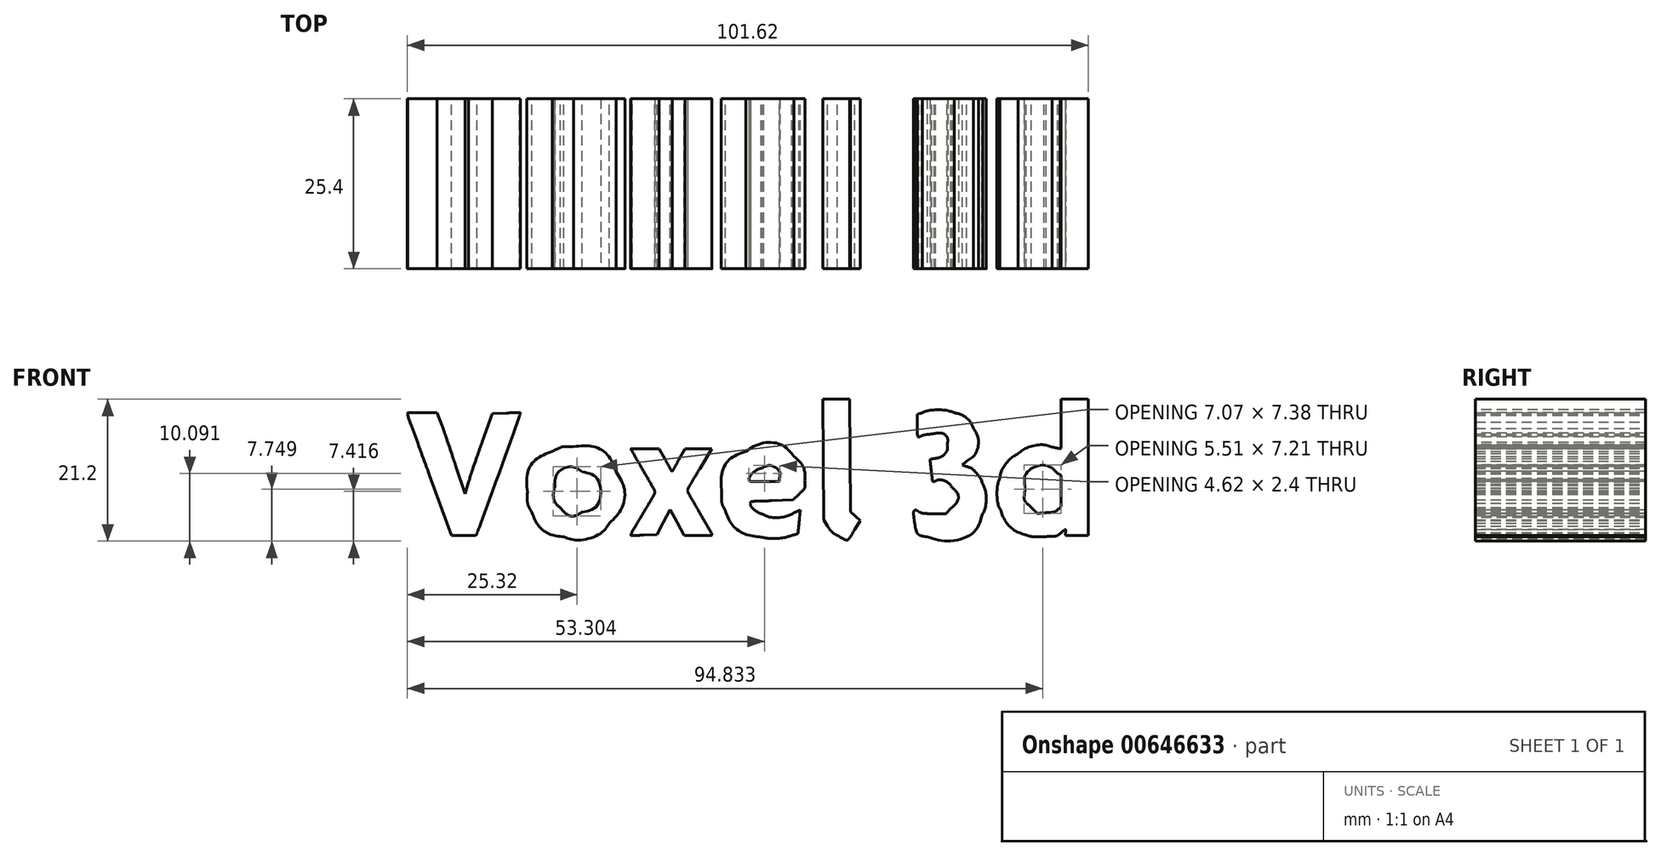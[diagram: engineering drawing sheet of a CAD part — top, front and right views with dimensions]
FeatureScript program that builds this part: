
annotation { "Feature Type Name" : "Feature", "Feature Type Description" : "" }
export const myFeature = defineFeature(function(context is Context, id is Id, definition is map)
    precondition{}
    {
        {
            var Q0;
            Q0=qCreatedBy(makeId("Front.planeOp"),FACE);
            var sketch = newSketch(context, id + "F0", { "sketchPlane" : qUnion([Q0])});
            skFitSpline(sketch, "E0", {"points": [v(-27.45, -20.66) * mm, v(-29.62, -20.2) * mm, v(-31.25, -18.97) * mm, v(-32.22, -17.03) * mm]});
            skFitSpline(sketch, "E1", {"points": [v(-32.22, -17.03) * mm, v(-32.8, -15.86) * mm, v(-32.9, -15.42) * mm, v(-32.9, -13.96) * mm]});
            skFitSpline(sketch, "E2", {"points": [v(-32.9, -13.96) * mm, v(-32.89, -11.11) * mm, v(-31.65, -9.09) * mm, v(-29.17, -7.87) * mm]});
            skFitSpline(sketch, "E3", {"points": [v(-29.17, -7.87) * mm, v(-27.91, -7.25) * mm, v(-27.48, -7.15) * mm, v(-26, -7.15) * mm]});
            skFitSpline(sketch, "E4", {"points": [v(-26, -7.15) * mm, v(-23.06, -7.15) * mm, v(-20.9, -8.43) * mm, v(-19.68, -10.91) * mm]});
            skFitSpline(sketch, "E5", {"points": [v(-19.68, -10.91) * mm, v(-18.45, -13.43) * mm, v(-18.83, -16.4) * mm, v(-20.68, -18.58) * mm]});
            skFitSpline(sketch, "E6", {"points": [v(-20.68, -18.58) * mm, v(-21.99, -20.12) * mm, v(-25.23, -21.12) * mm, v(-27.45, -20.66) * mm]});
            skFitSpline(sketch, "E7", {"points": [v(-24.71, -16.94) * mm, v(-22.4, -15.85) * mm, v(-22.43, -12.03) * mm, v(-24.75, -10.93) * mm]});
            skFitSpline(sketch, "E8", {"points": [v(-24.75, -10.93) * mm, v(-26.41, -10.14) * mm, v(-28.44, -11.17) * mm, v(-28.78, -12.97) * mm]});
            skFitSpline(sketch, "E9", {"points": [v(-28.78, -12.97) * mm, v(-29.04, -14.33) * mm, v(-28.75, -15.5) * mm, v(-27.96, -16.3) * mm]});
            skFitSpline(sketch, "E10", {"points": [v(-27.96, -16.3) * mm, v(-26.97, -17.33) * mm, v(-25.95, -17.53) * mm, v(-24.71, -16.94) * mm]});
            skFitSpline(sketch, "E11", {"points": [v(1.98, -20.67) * mm, v(-0.45, -20.22) * mm, v(-2.35, -18.82) * mm, v(-3.37, -16.72) * mm]});
            skFitSpline(sketch, "E12", {"points": [v(-3.37, -16.72) * mm, v(-3.8, -15.85) * mm, v(-3.9, -15.28) * mm, v(-3.9, -13.94) * mm]});
            skFitSpline(sketch, "E13", {"points": [v(-3.9, -13.94) * mm, v(-3.87, -11.07) * mm, v(-2.66, -9.03) * mm, v(-0.3, -7.86) * mm]});
            skFitSpline(sketch, "E14", {"points": [v(-0.3, -7.86) * mm, v(2.2, -6.63) * mm, v(5.12, -6.94) * mm, v(6.9, -8.64) * mm]});
            skFitSpline(sketch, "E15", {"points": [v(6.9, -8.64) * mm, v(7.92, -9.6) * mm, v(8.49, -10.9) * mm, v(8.5, -12.27) * mm]});
            skFitSpline(sketch, "E16", {"points": [v(8.5, -12.27) * mm, v(8.5, -13.3) * mm, v(8.42, -13.49) * mm, v(7.62, -14.26) * mm]});
            skFitSpline(sketch, "E17", {"points": [v(3.6, -15.23) * mm, v(1.4, -15.31) * mm, v(0.44, -15.43) * mm, v(0.44, -15.61) * mm]});
            skFitSpline(sketch, "E18", {"points": [v(0.44, -15.61) * mm, v(0.44, -16) * mm, v(1.58, -17.01) * mm, v(2.35, -17.3) * mm]});
            skFitSpline(sketch, "E19", {"points": [v(2.35, -17.3) * mm, v(3.41, -17.7) * mm, v(5.69, -17.6) * mm, v(6.84, -17.09) * mm]});
            skLineSegment(sketch, "E20", {"start": v(7.62, -14.26) * mm, "end": v(6.74, -15.12) * mm});
            skLineSegment(sketch, "E21", {"start": v(6.74, -15.12) * mm, "end": v(3.6, -15.23) * mm});
            skFitSpline(sketch, "E22", {"points": [v(7.72, -17.92) * mm, v(7.48, -20.1) * mm, v(7.45, -20.17) * mm, v(6.54, -20.43) * mm]});
            skFitSpline(sketch, "E23", {"points": [v(6.54, -20.43) * mm, v(5.34, -20.77) * mm, v(3.18, -20.88) * mm, v(1.98, -20.67) * mm]});
            skLineSegment(sketch, "E24", {"start": v(6.84, -17.09) * mm, "end": v(7.86, -16.64) * mm});
            skLineSegment(sketch, "E25", {"start": v(7.86, -16.64) * mm, "end": v(7.72, -17.92) * mm});
            skFitSpline(sketch, "E26", {"points": [v(4.7, -11.98) * mm, v(4.7, -10.83) * mm, v(3.31, -9.97) * mm, v(2.1, -10.37) * mm]});
            skFitSpline(sketch, "E27", {"points": [v(2.1, -10.37) * mm, v(1.4, -10.6) * mm, v(0.22, -11.73) * mm, v(0.22, -12.17) * mm]});
            skFitSpline(sketch, "E28", {"points": [v(0.22, -12.17) * mm, v(0.22, -12.28) * mm, v(1.23, -12.38) * mm, v(2.46, -12.38) * mm]});
            skFitSpline(sketch, "E29", {"points": [v(2.46, -12.38) * mm, v(4.45, -12.38) * mm, v(4.7, -12.33) * mm, v(4.7, -11.98) * mm]});
            skFitSpline(sketch, "E30", {"points": [v(13.37, -20.42) * mm, v(12.9, -20.17) * mm, v(12.25, -19.56) * mm, v(11.91, -19.04) * mm]});
            skFitSpline(sketch, "E31", {"points": [v(15.96, -19.55) * mm, v(15, -21.03) * mm, v(14.7, -21.13) * mm, v(13.37, -20.42) * mm]});
            skLineSegment(sketch, "E32", {"start": v(11.91, -19.04) * mm, "end": v(11.3, -18.12) * mm});
            skLineSegment(sketch, "E33", {"start": v(11.3, -18.12) * mm, "end": v(11.23, -9.1) * mm});
            skLineSegment(sketch, "E34", {"start": v(11.23, -9.1) * mm, "end": v(11.17, -0.07) * mm});
            skLineSegment(sketch, "E35", {"start": v(11.17, -0.07) * mm, "end": v(13.18, -0.07) * mm});
            skLineSegment(sketch, "E36", {"start": v(13.18, -0.07) * mm, "end": v(15.2, -0.07) * mm});
            skLineSegment(sketch, "E37", {"start": v(15.2, -0.07) * mm, "end": v(15.26, -8.48) * mm});
            skLineSegment(sketch, "E38", {"start": v(15.26, -8.48) * mm, "end": v(15.33, -16.89) * mm});
            skLineSegment(sketch, "E39", {"start": v(15.33, -16.89) * mm, "end": v(16.07, -17.55) * mm});
            skLineSegment(sketch, "E40", {"start": v(16.07, -17.55) * mm, "end": v(16.81, -18.22) * mm});
            skLineSegment(sketch, "E41", {"start": v(16.81, -18.22) * mm, "end": v(15.96, -19.55) * mm});
            skFitSpline(sketch, "E42", {"points": [v(26.76, -20.65) * mm, v(26.16, -20.55) * mm, v(25.58, -20.37) * mm, v(25.46, -20.25) * mm]});
            skFitSpline(sketch, "E43", {"points": [v(25.46, -20.25) * mm, v(25.24, -20.03) * mm, v(24.77, -16.84) * mm, v(24.93, -16.68) * mm]});
            skFitSpline(sketch, "E44", {"points": [v(24.93, -16.68) * mm, v(24.98, -16.63) * mm, v(25.26, -16.72) * mm, v(25.54, -16.88) * mm]});
            skFitSpline(sketch, "E45", {"points": [v(25.54, -16.88) * mm, v(25.84, -17.04) * mm, v(26.84, -17.17) * mm, v(27.82, -17.18) * mm]});
            skFitSpline(sketch, "E46", {"points": [v(27.82, -17.18) * mm, v(29.56, -17.19) * mm, v(29.57, -17.18) * mm, v(30.34, -16.35) * mm]});
            skFitSpline(sketch, "E47", {"points": [v(30.34, -16.35) * mm, v(31.3, -15.3) * mm, v(31.37, -14.29) * mm, v(30.53, -13.3) * mm]});
            skFitSpline(sketch, "E48", {"points": [v(30.53, -13.3) * mm, v(29.93, -12.58) * mm, v(28.73, -12.11) * mm, v(28, -12.3) * mm]});
            skFitSpline(sketch, "E49", {"points": [v(28, -12.3) * mm, v(27.65, -12.4) * mm, v(27.57, -12.24) * mm, v(27.45, -11.22) * mm]});
            skFitSpline(sketch, "E50", {"points": [v(27.45, -11.22) * mm, v(27.21, -9.28) * mm, v(27.25, -9.08) * mm, v(27.84, -8.93) * mm]});
            skFitSpline(sketch, "E51", {"points": [v(27.84, -8.93) * mm, v(28.85, -8.68) * mm, v(29.76, -7.7) * mm, v(29.76, -6.89) * mm]});
            skFitSpline(sketch, "E52", {"points": [v(29.76, -6.89) * mm, v(29.76, -5.75) * mm, v(28.87, -5.14) * mm, v(27.41, -5.28) * mm]});
            skFitSpline(sketch, "E53", {"points": [v(27.41, -5.28) * mm, v(26.8, -5.33) * mm, v(26.13, -5.45) * mm, v(25.93, -5.53) * mm]});
            skFitSpline(sketch, "E54", {"points": [v(25.93, -5.53) * mm, v(25.48, -5.72) * mm, v(25.3, -5.12) * mm, v(25.29, -3.5) * mm]});
            skFitSpline(sketch, "E55", {"points": [v(25.29, -3.5) * mm, v(25.28, -2.38) * mm, v(25.3, -2.33) * mm, v(26.05, -2.09) * mm]});
            skFitSpline(sketch, "E56", {"points": [v(26.05, -2.09) * mm, v(27.1, -1.74) * mm, v(29.66, -1.74) * mm, v(30.81, -2.09) * mm]});
            skFitSpline(sketch, "E57", {"points": [v(30.81, -2.09) * mm, v(32, -2.44) * mm, v(33.17, -3.4) * mm, v(33.65, -4.4) * mm]});
            skFitSpline(sketch, "E58", {"points": [v(33.65, -4.4) * mm, v(34.4, -6) * mm, v(33.96, -8.23) * mm, v(32.65, -9.33) * mm]});
            skFitSpline(sketch, "E59", {"points": [v(32.68, -10.14) * mm, v(33.48, -10.47) * mm, v(34.62, -11.73) * mm, v(35.05, -12.74) * mm]});
            skFitSpline(sketch, "E60", {"points": [v(35.05, -12.74) * mm, v(35.5, -13.81) * mm, v(35.43, -16.32) * mm, v(34.93, -17.42) * mm]});
            skFitSpline(sketch, "E61", {"points": [v(34.93, -17.42) * mm, v(33.84, -19.83) * mm, v(30.22, -21.26) * mm, v(26.76, -20.65) * mm]});
            skLineSegment(sketch, "E62", {"start": v(32.65, -9.33) * mm, "end": v(32.02, -9.87) * mm});
            skLineSegment(sketch, "E63", {"start": v(32.02, -9.87) * mm, "end": v(32.68, -10.14) * mm});
            skFitSpline(sketch, "E64", {"points": [v(41.56, -20.35) * mm, v(39.93, -19.74) * mm, v(38.42, -18.26) * mm, v(37.71, -16.57) * mm]});
            skFitSpline(sketch, "E65", {"points": [v(37.71, -16.57) * mm, v(37.32, -15.63) * mm, v(37.26, -13.12) * mm, v(37.6, -11.89) * mm]});
            skFitSpline(sketch, "E66", {"points": [v(37.6, -11.89) * mm, v(37.96, -10.6) * mm, v(39.17, -8.98) * mm, v(40.36, -8.2) * mm]});
            skFitSpline(sketch, "E67", {"points": [v(40.36, -8.2) * mm, v(41.73, -7.3) * mm, v(43.95, -6.87) * mm, v(45.43, -7.21) * mm]});
            skFitSpline(sketch, "E68", {"points": [v(45.43, -7.21) * mm, v(45.98, -7.34) * mm, v(46.5, -7.44) * mm, v(46.6, -7.45) * mm]});
            skFitSpline(sketch, "E69", {"points": [v(46.6, -7.45) * mm, v(46.7, -7.45) * mm, v(46.77, -5.8) * mm, v(46.77, -3.76) * mm]});
            skLineSegment(sketch, "E70", {"start": v(26.76, -20.65) * mm, "end": v(26.76, -20.65) * mm});
            skFitSpline(sketch, "E71", {"points": [v(49.12, -20.43) * mm, v(47.58, -20.43) * mm, v(47.44, -20.4) * mm, v(47.44, -19.98) * mm]});
            skFitSpline(sketch, "E72", {"points": [v(47.44, -19.98) * mm, v(47.44, -19.53) * mm, v(47.42, -19.53) * mm, v(46.75, -20.03) * mm]});
            skFitSpline(sketch, "E73", {"points": [v(46.75, -20.03) * mm, v(46.18, -20.45) * mm, v(45.73, -20.55) * mm, v(44.23, -20.6) * mm]});
            skFitSpline(sketch, "E74", {"points": [v(44.23, -20.6) * mm, v(43.09, -20.64) * mm, v(42.09, -20.54) * mm, v(41.56, -20.35) * mm]});
            skLineSegment(sketch, "E75", {"start": v(46.77, -3.76) * mm, "end": v(46.77, -0.07) * mm});
            skLineSegment(sketch, "E76", {"start": v(46.77, -0.07) * mm, "end": v(48.78, -0.07) * mm});
            skLineSegment(sketch, "E77", {"start": v(48.78, -0.07) * mm, "end": v(50.8, -0.07) * mm});
            skLineSegment(sketch, "E78", {"start": v(50.8, -0.07) * mm, "end": v(50.8, -10.25) * mm});
            skLineSegment(sketch, "E79", {"start": v(50.8, -10.25) * mm, "end": v(50.8, -20.43) * mm});
            skLineSegment(sketch, "E80", {"start": v(50.8, -20.43) * mm, "end": v(49.12, -20.43) * mm});
            skFitSpline(sketch, "E81", {"points": [v(46.31, -16.52) * mm, v(46.71, -16.16) * mm, v(46.77, -15.84) * mm, v(46.77, -13.8) * mm]});
            skFitSpline(sketch, "E82", {"points": [v(46.77, -13.8) * mm, v(46.77, -11.65) * mm, v(46.73, -11.47) * mm, v(46.26, -11.18) * mm]});
            skFitSpline(sketch, "E83", {"points": [v(46.26, -11.18) * mm, v(44.25, -9.92) * mm, v(41.57, -11.13) * mm, v(41.38, -13.39) * mm]});
            skFitSpline(sketch, "E84", {"points": [v(41.38, -13.39) * mm, v(41.26, -14.9) * mm, v(41.4, -15.34) * mm, v(42.3, -16.23) * mm]});
            skFitSpline(sketch, "E85", {"points": [v(42.3, -16.23) * mm, v(43.17, -17.11) * mm, v(43.21, -17.13) * mm, v(44.52, -17.03) * mm]});
            skFitSpline(sketch, "E86", {"points": [v(44.52, -17.03) * mm, v(45.4, -16.97) * mm, v(46.01, -16.8) * mm, v(46.31, -16.52) * mm]});
            skFitSpline(sketch, "E87", {"points": [v(-47.53, -11.42) * mm, v(-49.33, -6.47) * mm, v(-50.8, -2.34) * mm, v(-50.8, -2.25) * mm]});
            skFitSpline(sketch, "E88", {"points": [v(-50.8, -2.25) * mm, v(-50.8, -2.16) * mm, v(-49.8, -2.08) * mm, v(-48.59, -2.08) * mm]});
            skFitSpline(sketch, "E89", {"points": [v(-45.66, -4.04) * mm, v(-45.26, -5.12) * mm, v(-44.33, -7.85) * mm, v(-43.57, -10.1) * mm]});
            skLineSegment(sketch, "E90", {"start": v(-48.59, -2.08) * mm, "end": v(-46.37, -2.08) * mm});
            skLineSegment(sketch, "E91", {"start": v(-46.37, -2.08) * mm, "end": v(-45.66, -4.04) * mm});
            skFitSpline(sketch, "E92", {"points": [v(-41.68, -12.46) * mm, v(-41.39, -11.49) * mm, v(-40.48, -8.78) * mm, v(-39.66, -6.45) * mm]});
            skLineSegment(sketch, "E93", {"start": v(-43.57, -10.1) * mm, "end": v(-42.2, -14.21) * mm});
            skLineSegment(sketch, "E94", {"start": v(-42.2, -14.21) * mm, "end": v(-41.68, -12.46) * mm});
            skFitSpline(sketch, "E95", {"points": [v(-36.06, -2.13) * mm, v(-34.14, -2.07) * mm, v(-33.97, -2.1) * mm, v(-34.07, -2.46) * mm]});
            skFitSpline(sketch, "E96", {"points": [v(-34.07, -2.46) * mm, v(-34.15, -2.77) * mm, v(-39.95, -18.83) * mm, v(-40.45, -20.15) * mm]});
            skFitSpline(sketch, "E97", {"points": [v(-40.45, -20.15) * mm, v(-40.52, -20.35) * mm, v(-41.13, -20.43) * mm, v(-42.4, -20.43) * mm]});
            skLineSegment(sketch, "E98", {"start": v(-39.66, -6.45) * mm, "end": v(-38.16, -2.2) * mm});
            skLineSegment(sketch, "E99", {"start": v(-38.16, -2.2) * mm, "end": v(-36.06, -2.13) * mm});
            skFitSpline(sketch, "E100", {"points": [v(-17.46, -20.32) * mm, v(-17.46, -20.24) * mm, v(-16.65, -18.83) * mm, v(-15.67, -17.17) * mm]});
            skFitSpline(sketch, "E101", {"points": [v(-15.67, -17.17) * mm, v(-14.68, -15.52) * mm, v(-13.88, -14.08) * mm, v(-13.88, -13.96) * mm]});
            skFitSpline(sketch, "E102", {"points": [v(-13.88, -13.96) * mm, v(-13.88, -13.85) * mm, v(-14.6, -12.52) * mm, v(-15.47, -11) * mm]});
            skFitSpline(sketch, "E103", {"points": [v(-15.47, -11) * mm, v(-16.34, -9.48) * mm, v(-17.15, -8.06) * mm, v(-17.26, -7.84) * mm]});
            skFitSpline(sketch, "E104", {"points": [v(-17.26, -7.84) * mm, v(-17.46, -7.48) * mm, v(-17.3, -7.45) * mm, v(-15.36, -7.45) * mm]});
            skLineSegment(sketch, "E105", {"start": v(-42.4, -20.43) * mm, "end": v(-44.25, -20.43) * mm});
            skLineSegment(sketch, "E106", {"start": v(-44.25, -20.43) * mm, "end": v(-47.53, -11.42) * mm});
            skFitSpline(sketch, "E107", {"points": [v(-12.31, -9.13) * mm, v(-11.8, -10.05) * mm, v(-11.35, -10.8) * mm, v(-11.3, -10.8) * mm]});
            skFitSpline(sketch, "E108", {"points": [v(-11.3, -10.8) * mm, v(-11.26, -10.8) * mm, v(-10.8, -10.05) * mm, v(-10.3, -9.13) * mm]});
            skLineSegment(sketch, "E109", {"start": v(-15.36, -7.45) * mm, "end": v(-13.24, -7.45) * mm});
            skLineSegment(sketch, "E110", {"start": v(-13.24, -7.45) * mm, "end": v(-12.31, -9.13) * mm});
            skFitSpline(sketch, "E111", {"points": [v(-7.18, -10.44) * mm, v(-8.16, -12.09) * mm, v(-8.96, -13.55) * mm, v(-8.96, -13.7) * mm]});
            skFitSpline(sketch, "E112", {"points": [v(-8.96, -13.7) * mm, v(-8.96, -13.84) * mm, v(-8.15, -15.36) * mm, v(-7.17, -17.08) * mm]});
            skFitSpline(sketch, "E113", {"points": [v(-7.17, -17.08) * mm, v(-6.18, -18.79) * mm, v(-5.37, -20.24) * mm, v(-5.37, -20.31) * mm]});
            skFitSpline(sketch, "E114", {"points": [v(-5.37, -20.31) * mm, v(-5.37, -20.38) * mm, v(-6.3, -20.43) * mm, v(-7.45, -20.43) * mm]});
            skLineSegment(sketch, "E115", {"start": v(-10.3, -9.13) * mm, "end": v(-9.37, -7.45) * mm});
            skLineSegment(sketch, "E116", {"start": v(-9.37, -7.45) * mm, "end": v(-7.39, -7.45) * mm});
            skLineSegment(sketch, "E117", {"start": v(-7.39, -7.45) * mm, "end": v(-5.4, -7.45) * mm});
            skLineSegment(sketch, "E118", {"start": v(-5.4, -7.45) * mm, "end": v(-7.18, -10.44) * mm});
            skFitSpline(sketch, "E119", {"points": [v(-15.53, -20.39) * mm, v(-16.59, -20.42) * mm, v(-17.46, -20.39) * mm, v(-17.46, -20.32) * mm]});
            skLineSegment(sketch, "E120", {"start": v(-7.45, -20.43) * mm, "end": v(-9.52, -20.43) * mm});
            skLineSegment(sketch, "E121", {"start": v(-9.52, -20.43) * mm, "end": v(-10.55, -18.51) * mm});
            skLineSegment(sketch, "E122", {"start": v(-10.55, -18.51) * mm, "end": v(-11.58, -16.59) * mm});
            skLineSegment(sketch, "E123", {"start": v(-11.58, -16.59) * mm, "end": v(-12.59, -18.45) * mm});
            skLineSegment(sketch, "E124", {"start": v(-12.59, -18.45) * mm, "end": v(-13.6, -20.32) * mm});
            skLineSegment(sketch, "E125", {"start": v(-13.6, -20.32) * mm, "end": v(-15.53, -20.39) * mm});
            skSolve(sketch);
        }
        {
            var Q0;
            Q0 = qSketchRegion(id + "F0", true);
            extrude(context, id + "F1", {"entities" : qUnion([Q0]), "depth" : 25.4 * mm, "offsetDistance" : 25.4 * mm});
        }
    });
